# Revit family: Water_Boiler-Navien-NFB-Condensing-02
name_source: partatom
category: Mechanical Equipment
revit_build: Autodesk Revit 2016 (Build: 20150220_1215(x64)
units: mm (PartAtom-declared; Revit-internal decimal feet)

## family parameters
Cut with Voids When Loaded = No
Host = Face
OmniClass Number = 23.65.35.11
OmniClass Title = Supply Water Heaters
Part Type = Normal
Room Calculation Point = No
Round Connector Dimension = Use Diameter
Shared = No

## types (1)
- NFB-175
    2" Exhaust/Intake = Yes
    3" Exhaust/Intake = No
    Apparent Load = 0 VA
    Assembly Code = D3010500
    Certifications = Energy Star | AHRI | CSA | ASME | CSA Blue Star | CSA Blue Flame
    Cold Water Inlet = 1"
    Default Elevation = 4' - 0"
    Depth = 1' - 5 5/16"
    Description = NFB High-Efficiency Condensing Fire Tube Boiler
    Exhaust = 2"
    Finish = Metal - Navien - White
    Flow Rate = 0 GPM
    Frequency = 60 Hz
    Gas Inlet = 1"
    Heating Capacity = 175000.0 Btu/h
    Heating Capacity Note = 17,500–175,000(BTU/H)
    Height = 2' - 3 19/32"
    Hot Water Outlet = 1"
    Ignition = Electronic ignition
    Installation Type = Indoor Wall-Hung
    Intake = 2"
    Keynote = 22 33 00.A1
    Manufacturer = Navien, Inc.
    Manufacturer Fax Number = (949) 420-0430
    Model = NFB-175
    Natural Gas Manifold Pressure = -0.05" to -0.70" WC
    Natural Gas Supply Pressure = 3.5" to 10.5" WC
    Number of Poles = 1
    Phase = 1
    Power Factor = 1
    Product Documentation Link = https://www.navieninc.com
    Product Name = NFB Series Condensing Boiler
    Product Page URL = https://www.navieninc.com
    Propane Gas Manifold Pressure = -0.10" to -0.68" WC
    Propane Gas Supply Pressure = 8.0" to 13.5" WC
    Recirculation Inlet = 1"
    URL = https://www.navieninc.com
    Venting = PVC, CPVC, PP | Size (2in) | Length (60 ft)
    Venting Type = Forced draft direct vent
    Version = 2016 - v1.0.a
    Voltage = 120 V
    Warranty = https://www.navieninc.com
    Warranty Note = Heat Exchangers: 15 years limited warranty (Residential), 10 years (Commercial) | Parts: 5 years (Residential), 3 years (Commercial) | Labor: 1 year (Residential), 1 year (Commercial)
    Water Pressure = 12–80 psi
    Weight = 123.00 lbf
    Wi-Fi Ready = NaviLink Wi‑Fi Control: This add-on accessory enables access to control temperatures remotely, access usage data and receive diagnostic notifications via smartphone or tablet.
    Width = 1' - 5 5/16"

## geometry (parser evidence)
native form markers: Sweep x5
no freeform markers — native parametric forms only
